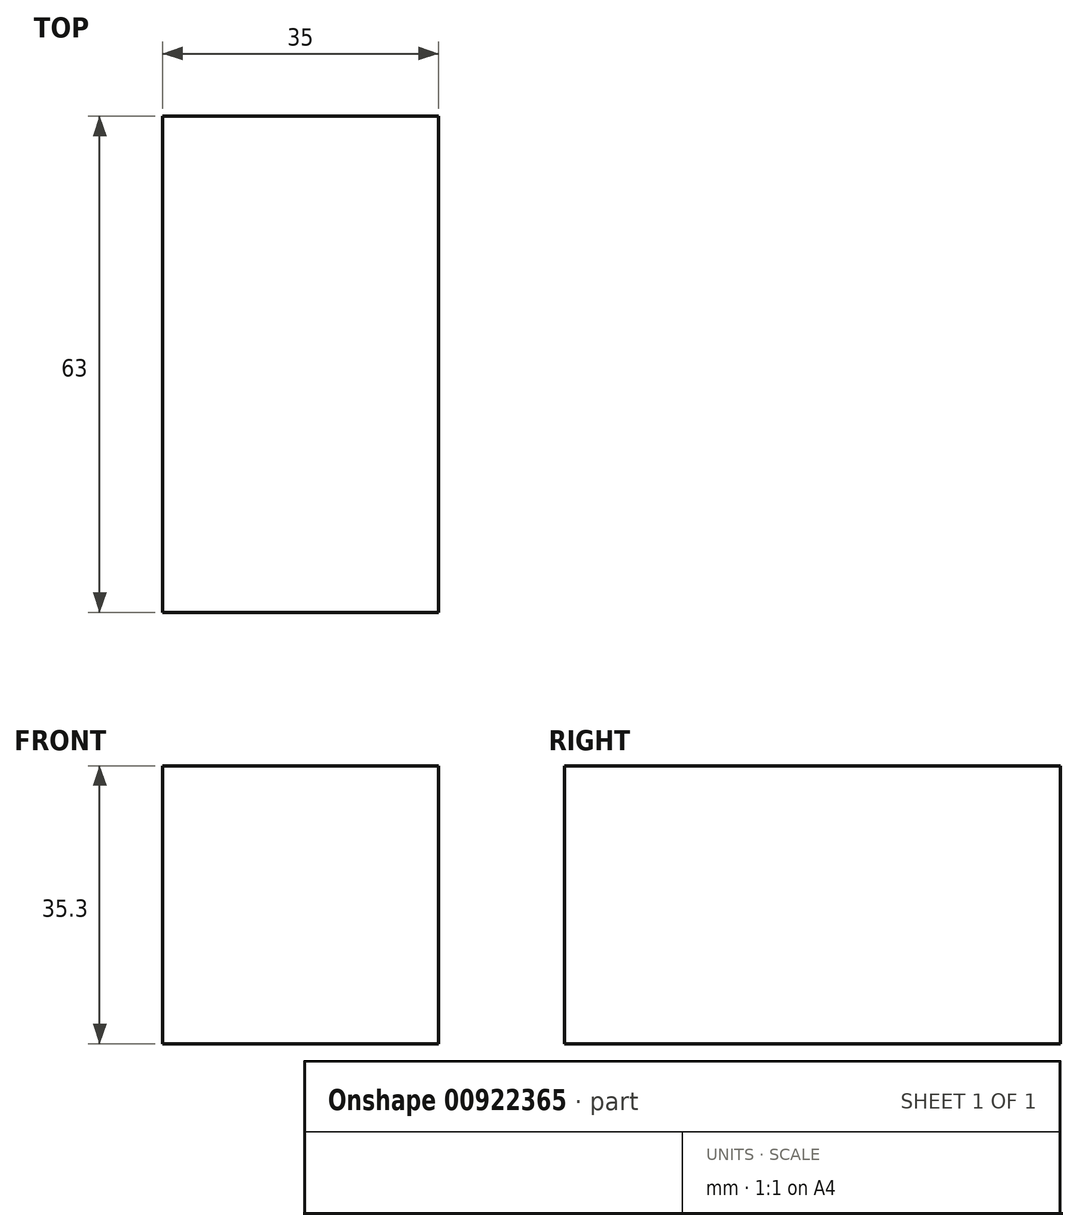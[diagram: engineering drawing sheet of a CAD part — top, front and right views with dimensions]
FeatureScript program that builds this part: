
annotation { "Feature Type Name" : "Feature", "Feature Type Description" : "" }
export const myFeature = defineFeature(function(context is Context, id is Id, definition is map)
    precondition{}
    {
        {
            var Q0;
            Q0=qCreatedBy(makeId("Top.planeOp"),FACE);
            var sketch = newSketch(context, id + "F0", { "sketchPlane" : qUnion([Q0])});
            skLineSegment(sketch, "E0", {"start": v(0, 0.33) * mm, "end": v(0, -49.67) * mm});
            skLineSegment(sketch, "E1.bottom", {"start": v(-17.5, -49.67) * mm, "end": v(17.5, -49.67) * mm});
            skLineSegment(sketch, "E1.top", {"start": v(-17.5, -112.67) * mm, "end": v(17.5, -112.67) * mm});
            skLineSegment(sketch, "E1.left", {"start": v(-17.5, -49.67) * mm, "end": v(-17.5, -112.67) * mm});
            skLineSegment(sketch, "E1.right", {"start": v(17.5, -49.67) * mm, "end": v(17.5, -112.67) * mm});
            skSolve(sketch);
        }
        {
            var Q0;
            Q0 = qSketchRegion(id + "F0", true);
            extrude(context, id + "F1", {"entities" : qUnion([Q0]), "depth" : 35.3 * mm, "offsetDistance" : 25 * mm});
        }
    });
